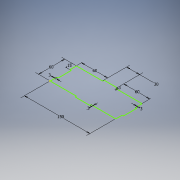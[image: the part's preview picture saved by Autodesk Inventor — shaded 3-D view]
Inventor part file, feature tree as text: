
AUTODESK INVENTOR PART (.ipt)
format: ipt  version: 2017 (Build 210142000, 142)  size: 96,768 bytes
history: native  units: mm
features: sketch x1
ambient origin geometry x8: Origin, YZ Plane, XZ Plane, XY Plane, X Axis, Y Axis, Z Axis, Center Point
feature tree (1):
  sketch  "Sketch1"  dims[d0=3.0mm d1=150.0mm d2=60.0mm d3=30.0mm d4=60.0mm d5=60.0mm d6=3.0mm d7=15.0mm d8=3.0mm d9=3.0mm]
